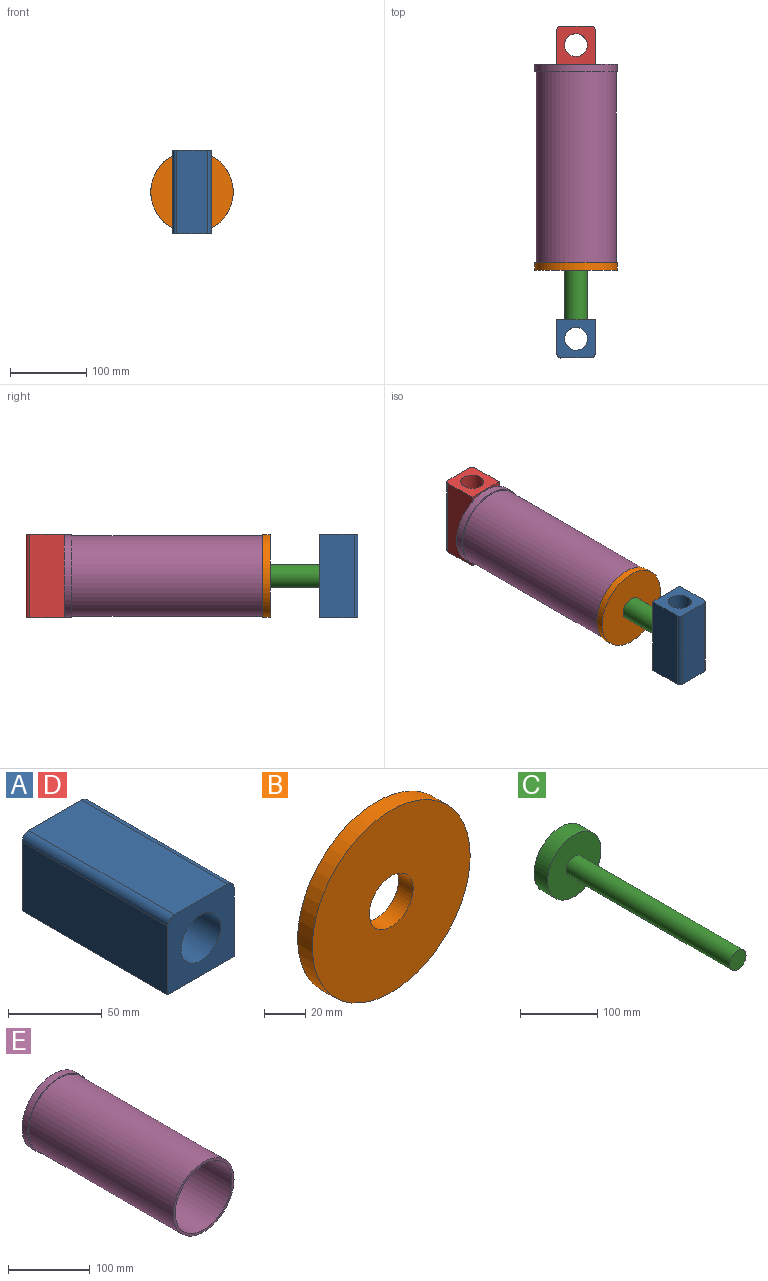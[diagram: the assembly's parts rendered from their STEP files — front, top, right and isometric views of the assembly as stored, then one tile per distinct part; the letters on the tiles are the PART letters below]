
ASSEMBLY  parts=5 mates=4
PART A: 9 faces, bbox 50x110x50 mm
  f0: plane 110x45mm, normal (-1,0,0), area 4950mm2, adj f1,f5,f6,f8
  f1: plane 110x50mm, normal (0,0,-1), area 5500mm2, adj f0,f2,f5,f6
  f2: plane 110x45mm, normal (1,0,0), area 4950mm2, adj f1,f5,f6,f7
  f3: cylinder r=15mm len=110mm, axis (0,1,0), area 10367.3mm2, adj f5,f6
  f4: plane 110x40mm, normal (0,0,1), area 4400mm2, adj f5,f6,f7,f8
  f5: plane 50x50mm, normal (0,-1,0), area 1782.4mm2, adj f0,f1,f2,f3,f4,f7,f8
  f6: plane 50x50mm, normal (0,1,0), area 1782.4mm2, adj f0,f1,f2,f3,f4,f7,f8
  f7: cylinder r=5mm len=110mm, axis (0,1,0), area 863.9mm2, adj f2,f4,f5,f6
  f8: cylinder r=5mm len=110mm, axis (0,-1,0), area 863.9mm2, adj f0,f4,f5,f6
PART B: 4 faces, bbox 108x10x108 mm
  f0: cylinder r=15mm len=30mm, axis (0,1,0), area 942.5mm2, adj f2,f3
  f1: cylinder r=54mm len=108mm, axis (0,1,0), area 3392.9mm2, adj f2,f3
  f2: plane 108x108mm, normal (0,-1,0), area 8454mm2, adj f0,f1
  f3: plane 108x108mm, normal (0,1,0), area 8454mm2, adj f0,f1
PART C: 5 faces, bbox 98x325x98 mm
  f0: cylinder r=15mm len=300mm, axis (0,1,0), area 28274.3mm2, adj f1,f4
  f1: plane 30x30mm, normal (0,-1,0), area 706.9mm2, adj f0
  f2: cylinder r=49mm len=98mm, axis (0,-1,0), area 7696.9mm2, adj f3,f4
  f3: plane 98x98mm, normal (0,1,0), area 7543mm2, adj f2
  f4: plane 98x98mm, normal (0,-1,0), area 6836.1mm2, adj f0,f2
PART D: same geometry as A
PART E: 7 faces, bbox 108x260x108 mm
  f0: cylinder r=49mm len=250mm, axis (0,1,0), area 76969mm2, adj f2,f6
  f1: cylinder r=52.5mm len=250mm, axis (0,1,0), area 82466.8mm2, adj f2,f3
  f2: plane 105x105mm, normal (0,-1,0), area 1116.1mm2, adj f0,f1
  f3: plane 108x108mm, normal (0,-1,0), area 501.9mm2, adj f1,f5
  f4: plane 108x108mm, normal (0,1,0), area 9160.9mm2, adj f5
  f5: cylinder r=54mm len=108mm, axis (0,-1,0), area 3392.9mm2, adj f3,f4
  f6: plane 98x98mm, normal (0,-1,0), area 7543mm2, adj f0
PLACE A rot(axis=(1,0,0),90deg) t=(-3.43,113.71,80.49)mm
PLACE B rot(axis=(0,-1,0),0deg) t=(42.34,202.89,-15.76)mm
PLACE C rot(axis=(0,-1,0),0deg) t=(29.66,427.89,2.5)mm
PLACE D rot(axis=(0,0.71,0.71),180deg) t=(-37.6,477.07,80.49)mm
PLACE E t=(14.19,452.89,-15.33)mm
MATE fastened D.f1 <-> E.f0  axis (0,-1,0) through (-20.51,462.89,25.49)mm
MATE fastened A.f1 <-> C.f0  axis (0,1,0) through (-20.51,127.89,25.49)mm
MATE fastened E.f0 <-> B.f0  axis (0,1,0) through (-20.51,202.89,25.49)mm
MATE slider C.f0 <-> E.f0  axis (0,-1,0) through (-20.51,427.89,25.49)mm
